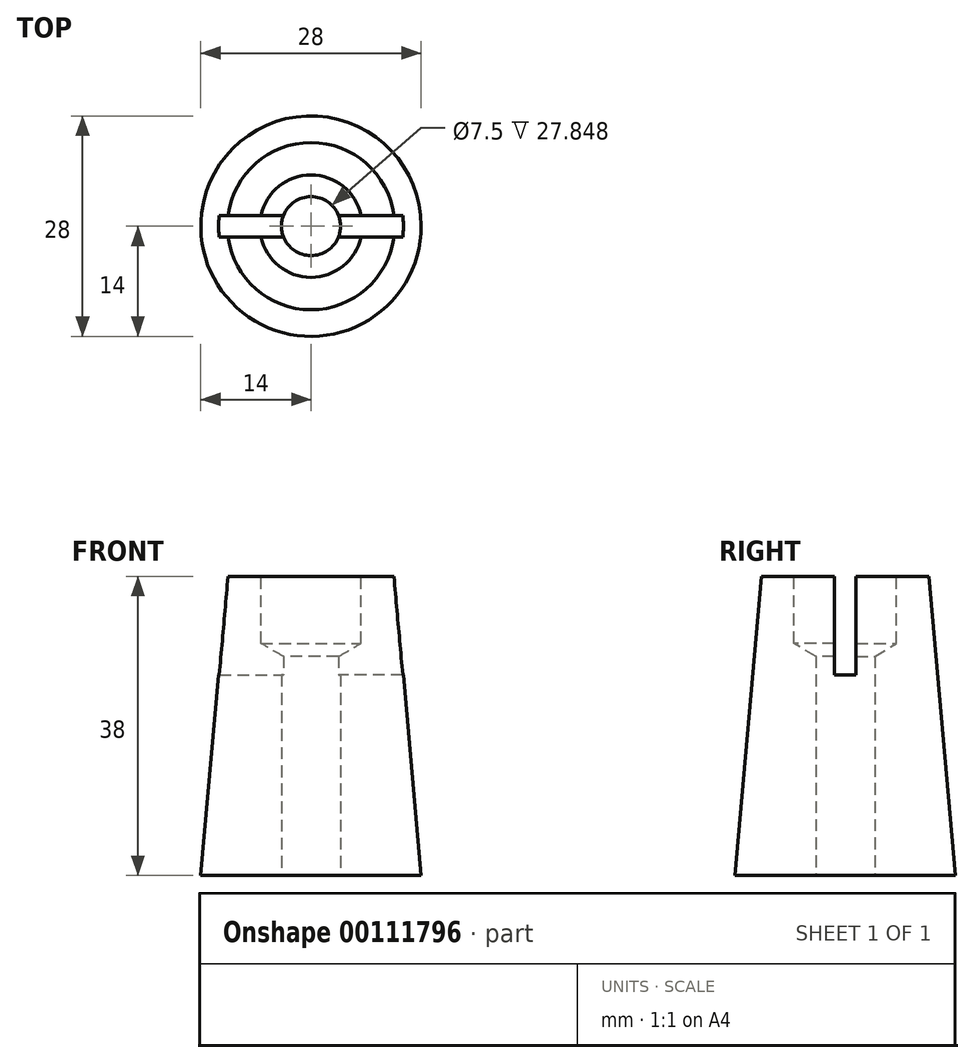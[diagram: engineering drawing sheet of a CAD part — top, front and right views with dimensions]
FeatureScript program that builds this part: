
annotation { "Feature Type Name" : "Feature", "Feature Type Description" : "" }
export const myFeature = defineFeature(function(context is Context, id is Id, definition is map)
    precondition{}
    {
        {
            var Q0;
            Q0=qCreatedBy(makeId("Top.planeOp"),FACE);
            var sketch = newSketch(context, id + "F0", { "sketchPlane" : qUnion([Q0])});
            skCircle(sketch, "E0", {"center": v(0, 0) * mm, "radius": 14 * mm});
            skSolve(sketch);
        }
        {
            var Q0;
            Q0=qCreatedBy(makeId("Top.planeOp"),FACE);
            cPlane(context, id + "F1", {"entities" : qUnion([Q0]), "cplaneType" : CPlaneType.OFFSET, "offset" : 38 * mm, "width" : 150 * mm, "height" : 150 * mm});
        }
        {
            var Q0;
            Q0=qCreatedBy(id+"F1.planeOp",FACE);
            var sketch = newSketch(context, id + "F2", { "sketchPlane" : qUnion([Q0])});
            skCircle(sketch, "E1", {"center": v(0, 0) * mm, "radius": 10.62 * mm});
            skSolve(sketch);
        }
        {
            var Q0;
            Q0=makeQuery(id+"F2.imprint","IMPRINT",FACE,{"disambiguationData":[TD([[makeQuery(id+"F2.imprint","IMPRINT",EDGE,{"derivedFrom":sQuery(id+"F2.wireOp",EDGE,"E1")}),1.0]])]});
            var Q1;
            Q1=makeQuery(id+"F0.imprint","IMPRINT",FACE,{"disambiguationData":[TD([[makeQuery(id+"F0.imprint","IMPRINT",EDGE,{"derivedFrom":sQuery(id+"F0.wireOp",EDGE,"E0")}),1.0]])]});
            loft(context, id + "F3", {"sheetProfilesArray" : [{ "sheetProfileEntities" : qUnion([Q0]) }, { "sheetProfileEntities" : qUnion([Q1]) }]});
        }
        {
            var Q0;
            Q0=qCreatedBy(makeId("Top.planeOp"),FACE);
            var sketch = newSketch(context, id + "F4", { "sketchPlane" : qUnion([Q0])});
            skCircle(sketch, "E2", {"center": v(0, 0) * mm, "radius": 3.75 * mm});
            skSolve(sketch);
        }
        {
            var Q0;
            Q0=makeQuery(id+"F4.imprint","IMPRINT",FACE,{"disambiguationData":[TD([[makeQuery(id+"F4.imprint","IMPRINT",EDGE,{"derivedFrom":sQuery(id+"F4.wireOp",EDGE,"E2")}),1.0]])]});
            extrude(context, id + "F5", {"entities" : qUnion([Q0]), "operationType" : NewBodyOperationType.REMOVE, "depth" : 61.9 * mm});
        }
        {
            var Q0;
            Q0=makeQuery(id+"F3.opLoft","CAP_FACE",FACE,{"disambiguationData":[OSD([makeQuery(id+"F2.imprint","IMPRINT",FACE,{"disambiguationData":[TD([[makeQuery(id+"F2.imprint","IMPRINT",EDGE,{"derivedFrom":sQuery(id+"F2.wireOp",EDGE,"E1")}),1.0]])]})])],"isStart":true});
            var sketch = newSketch(context, id + "F6", { "sketchPlane" : qUnion([Q0])});
            skLineSegment(sketch, "E3", {"start": v(-16.09, 1.37) * mm, "end": v(16.65, 1.38) * mm});
            skLineSegment(sketch, "E4", {"start": v(16.65, 1.38) * mm, "end": v(16.65, -1.37) * mm});
            skLineSegment(sketch, "E5", {"start": v(16.65, -1.37) * mm, "end": v(-16.09, -1.38) * mm});
            skLineSegment(sketch, "E6", {"start": v(-16.09, -1.38) * mm, "end": v(-16.09, 1.37) * mm});
            skLineSegment(sketch, "E7", {"start": v(-16.09, 0) * mm, "end": v(16.65, 0) * mm});
            skSolve(sketch);
        }
        {
            var Q0;
            {var subQ0=sQuery(id+"F6.wireOp",EDGE,"E4");var subQ1=sQuery(id+"F6.wireOp",EDGE,"E3");var subQ2=makeQuery(id+"F6.imprint","INTERSECT",VERTEX,{"derivedFrom":[subQ1,subQ0]});Q0=makeQuery(id+"F6.imprint","IMPRINT",FACE,{"disambiguationData":[TD([[makeQuery(id+"F6.imprint","IMPRINT",EDGE,{"disambiguationData":[TD([[subQ2,1.0]])],"derivedFrom":subQ1}),-1.0]])]});}
            var Q1;
            {var subQ0=sQuery(id+"F6.wireOp",EDGE,"E5");var subQ1=sQuery(id+"F6.wireOp",EDGE,"E4");var subQ2=makeQuery(id+"F6.imprint","INTERSECT",VERTEX,{"derivedFrom":[subQ1,subQ0]});Q1=makeQuery(id+"F6.imprint","IMPRINT",FACE,{"disambiguationData":[TD([[makeQuery(id+"F6.imprint","IMPRINT",EDGE,{"disambiguationData":[TD([[subQ2,1.0]])],"derivedFrom":subQ1}),-1.0]])]});}
            var Q2;
            {var subQ0=sQuery(id+"F6.wireOp",EDGE,"E5");var subQ1=sQuery(id+"F2.wireOp",EDGE,"E1");var subQ2=makeQuery(id+"F3.opLoft","MID_CAP_EDGE",EDGE,{"disambiguationData":[OSD([subQ1])],"capPos":0.0});var subQ3=makeQuery(id+"F6.imprint","INTERSECT",VERTEX,{"disambiguationData":[OD(0.0)],"derivedFrom":[subQ2,subQ0]});Q2=makeQuery(id+"F6.imprint","IMPRINT",FACE,{"disambiguationData":[TD([[makeQuery(id+"F6.imprint","IMPRINT",EDGE,{"disambiguationData":[TD([[subQ3,1.0]])],"derivedFrom":subQ2}),-1.0]])]});}
            var Q3;
            {var subQ0=sQuery(id+"F6.wireOp",EDGE,"E3");var subQ1=sQuery(id+"F2.wireOp",EDGE,"E1");var subQ2=makeQuery(id+"F3.opLoft","MID_CAP_EDGE",EDGE,{"disambiguationData":[OSD([subQ1])],"capPos":0.0});var subQ3=makeQuery(id+"F6.imprint","INTERSECT",VERTEX,{"disambiguationData":[OD(1.0)],"derivedFrom":[subQ2,subQ0]});Q3=makeQuery(id+"F6.imprint","IMPRINT",FACE,{"disambiguationData":[TD([[makeQuery(id+"F6.imprint","IMPRINT",EDGE,{"disambiguationData":[TD([[subQ3,-1.0]])],"derivedFrom":subQ2}),-1.0]])]});}
            var Q4;
            {var subQ0=sQuery(id+"F6.wireOp",EDGE,"E3");var subQ1=makeQuery(id+"F5.boolean.opBoolean","INTERSECT",EDGE,{"derivedFrom":[makeQuery(id+"F3.opLoft","CAP_FACE",FACE,{"disambiguationData":[OSD([makeQuery(id+"F2.imprint","IMPRINT",FACE,{"disambiguationData":[TD([[makeQuery(id+"F2.imprint","IMPRINT",EDGE,{"derivedFrom":sQuery(id+"F2.wireOp",EDGE,"E1")}),1.0]])]})])],"isStart":true}),makeQuery(id+"F5.opExtrude","SWEPT_FACE",FACE,{"disambiguationData":[OSD([sQuery(id+"F4.wireOp",EDGE,"E2")])]})]});var subQ2=makeQuery(id+"F6.imprint","INTERSECT",VERTEX,{"disambiguationData":[OD(0.0)],"derivedFrom":[subQ1,subQ0]});Q4=makeQuery(id+"F6.imprint","IMPRINT",FACE,{"disambiguationData":[TD([[makeQuery(id+"F6.imprint","IMPRINT",EDGE,{"disambiguationData":[TD([[subQ2,-1.0]])],"derivedFrom":subQ0}),-1.0]])]});}
            var Q5;
            {var subQ0=sQuery(id+"F6.wireOp",EDGE,"E5");var subQ1=makeQuery(id+"F5.boolean.opBoolean","INTERSECT",EDGE,{"derivedFrom":[makeQuery(id+"F3.opLoft","CAP_FACE",FACE,{"disambiguationData":[OSD([makeQuery(id+"F2.imprint","IMPRINT",FACE,{"disambiguationData":[TD([[makeQuery(id+"F2.imprint","IMPRINT",EDGE,{"derivedFrom":sQuery(id+"F2.wireOp",EDGE,"E1")}),1.0]])]})])],"isStart":true}),makeQuery(id+"F5.opExtrude","SWEPT_FACE",FACE,{"disambiguationData":[OSD([sQuery(id+"F4.wireOp",EDGE,"E2")])]})]});var subQ2=makeQuery(id+"F6.imprint","INTERSECT",VERTEX,{"disambiguationData":[OD(0.0)],"derivedFrom":[subQ1,subQ0]});Q5=makeQuery(id+"F6.imprint","IMPRINT",FACE,{"disambiguationData":[TD([[makeQuery(id+"F6.imprint","IMPRINT",EDGE,{"disambiguationData":[TD([[subQ2,-1.0]])],"derivedFrom":subQ0}),-1.0]])]});}
            var Q6;
            {var subQ0=sQuery(id+"F6.wireOp",EDGE,"E5");var subQ1=sQuery(id+"F2.wireOp",EDGE,"E1");var subQ2=makeQuery(id+"F3.opLoft","MID_CAP_EDGE",EDGE,{"disambiguationData":[OSD([subQ1])],"capPos":0.0});var subQ3=makeQuery(id+"F6.imprint","INTERSECT",VERTEX,{"disambiguationData":[OD(1.0)],"derivedFrom":[subQ2,subQ0]});Q6=makeQuery(id+"F6.imprint","IMPRINT",FACE,{"disambiguationData":[TD([[makeQuery(id+"F6.imprint","IMPRINT",EDGE,{"disambiguationData":[TD([[subQ3,-1.0]])],"derivedFrom":subQ2}),-1.0]])]});}
            var Q7;
            {var subQ0=sQuery(id+"F6.wireOp",EDGE,"E3");var subQ1=sQuery(id+"F2.wireOp",EDGE,"E1");var subQ2=makeQuery(id+"F3.opLoft","MID_CAP_EDGE",EDGE,{"disambiguationData":[OSD([subQ1])],"capPos":0.0});var subQ3=makeQuery(id+"F6.imprint","INTERSECT",VERTEX,{"disambiguationData":[OD(0.0)],"derivedFrom":[subQ2,subQ0]});Q7=makeQuery(id+"F6.imprint","IMPRINT",FACE,{"disambiguationData":[TD([[makeQuery(id+"F6.imprint","IMPRINT",EDGE,{"disambiguationData":[TD([[subQ3,1.0]])],"derivedFrom":subQ2}),-1.0]])]});}
            var Q8;
            {var subQ0=sQuery(id+"F6.wireOp",EDGE,"E6");var subQ1=sQuery(id+"F6.wireOp",EDGE,"E5");var subQ2=makeQuery(id+"F6.imprint","INTERSECT",VERTEX,{"derivedFrom":[subQ1,subQ0]});Q8=makeQuery(id+"F6.imprint","IMPRINT",FACE,{"disambiguationData":[TD([[makeQuery(id+"F6.imprint","IMPRINT",EDGE,{"disambiguationData":[TD([[subQ2,1.0]])],"derivedFrom":subQ1}),-1.0]])]});}
            var Q9;
            {var subQ0=sQuery(id+"F6.wireOp",EDGE,"E6");var subQ1=sQuery(id+"F6.wireOp",EDGE,"E3");var subQ2=makeQuery(id+"F6.imprint","INTERSECT",VERTEX,{"derivedFrom":[subQ1,subQ0]});Q9=makeQuery(id+"F6.imprint","IMPRINT",FACE,{"disambiguationData":[TD([[makeQuery(id+"F6.imprint","IMPRINT",EDGE,{"disambiguationData":[TD([[subQ2,-1.0]])],"derivedFrom":subQ1}),-1.0]])]});}
            extrude(context, id + "F7", {"entities" : qUnion([Q0, Q1, Q2, Q3, Q4, Q5, Q6, Q7, Q8, Q9]), "operationType" : NewBodyOperationType.REMOVE, "oppositeDirection" : true, "depth" : 12.5 * mm});
        }
        {
            var Q0;
            {var subQ0=sQuery(id+"F2.wireOp",EDGE,"E1");Q0=makeQuery(id+"F7.boolean.opBoolean","SPLIT",FACE,{"disambiguationData":[TD([makeQuery(id+"F7.opExtrude","SWEPT_FACE",FACE,{"disambiguationData":[OSD([sQuery(id+"F6.wireOp",EDGE,"E5")])]})])],"derivedFrom":makeQuery(id+"F3.opLoft","CAP_FACE",FACE,{"disambiguationData":[OSD([makeQuery(id+"F2.imprint","IMPRINT",FACE,{"disambiguationData":[TD([[makeQuery(id+"F2.imprint","IMPRINT",EDGE,{"derivedFrom":subQ0}),1.0]])]})])],"isStart":true})});}
            var sketch = newSketch(context, id + "F8", { "sketchPlane" : qUnion([Q0])});
            skPoint(sketch, "E8", {"position": v(0, 0) * mm});
            skSolve(sketch);
        }
        {
            var Q0;
            Q0=sQuery(id+"F8.wireOp",VERTEX,"E8");
            var Q1;
            Q1=makeQuery(id+"F3.opLoft","SWEPT_BODY",BODY,{"disambiguationData":[OSD([makeQuery(id+"F0.imprint","IMPRINT",FACE,{"disambiguationData":[TD([[makeQuery(id+"F0.imprint","IMPRINT",EDGE,{"derivedFrom":sQuery(id+"F0.wireOp",EDGE,"E0")}),1.0]])]}),makeQuery(id+"F2.imprint","IMPRINT",FACE,{"disambiguationData":[TD([[makeQuery(id+"F2.imprint","IMPRINT",EDGE,{"derivedFrom":sQuery(id+"F2.wireOp",EDGE,"E1")}),1.0]])]})])]});
            hole(context, id + "F9", {"style" : HoleStyle.SIMPLE, "endStyle" : HoleEndStyle.BLIND, "holeDiameter" : 13 * mm, "holeDepth" : 8.5 * mm, "startFromSketch" : true, "locations" : qUnion([Q0]), "scope" : qUnion([Q1])});
        }
    });
